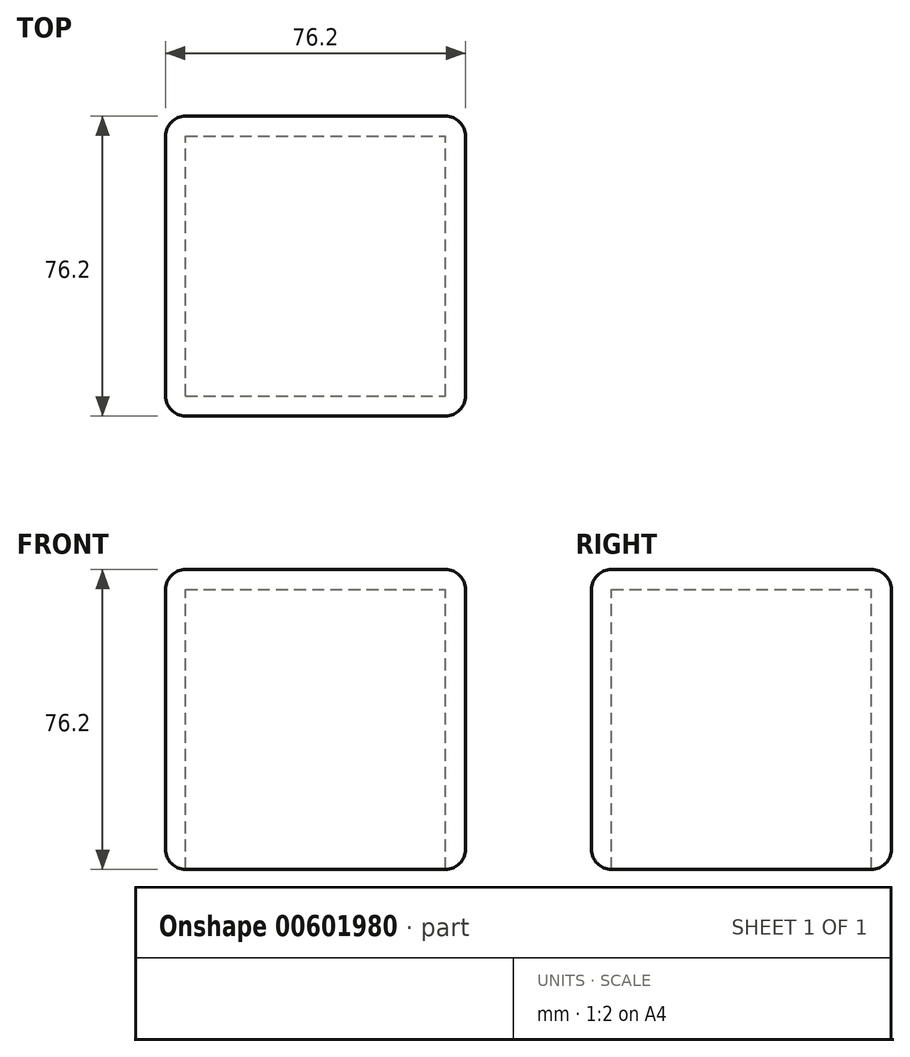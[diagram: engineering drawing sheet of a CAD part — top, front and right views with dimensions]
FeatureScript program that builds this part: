
annotation { "Feature Type Name" : "Feature", "Feature Type Description" : "" }
export const myFeature = defineFeature(function(context is Context, id is Id, definition is map)
    precondition{}
    {
        {
            var Q0;
            Q0=qCreatedBy(makeId("Front.planeOp"),FACE);
            var sketch = newSketch(context, id + "F0", { "sketchPlane" : qUnion([Q0])});
            skLineSegment(sketch, "E0.bottom", {"start": v(0, 0) * mm, "end": v(76.2, 0) * mm});
            skLineSegment(sketch, "E0.top", {"start": v(0, 76.2) * mm, "end": v(76.2, 76.2) * mm});
            skLineSegment(sketch, "E0.left", {"start": v(0, 0) * mm, "end": v(0, 76.2) * mm});
            skLineSegment(sketch, "E0.right", {"start": v(76.2, 0) * mm, "end": v(76.2, 76.2) * mm});
            skSolve(sketch);
        }
        {
            var Q0;
            Q0=makeQuery(id+"F0.imprint","IMPRINT",FACE,{"disambiguationData":[TD([[makeQuery(id+"F0.imprint","IMPRINT",EDGE,{"derivedFrom":sQuery(id+"F0.wireOp",EDGE,"E0.bottom")}),1.0]])]});
            extrude(context, id + "F1", {"entities" : qUnion([Q0]), "depth" : 76.2 * mm, "offsetDistance" : 25.4 * mm});
        }
        {
            var Q0;
            Q0=makeQuery(id+"F1.opExtrude","SWEPT_FACE",FACE,{"disambiguationData":[OSD([sQuery(id+"F0.wireOp",EDGE,"E0.bottom")])]});
            shell(context, id + "F2", {"entities" : qUnion([Q0]), "thickness" : 5.08 * mm});
        }
        {
            var Q0;
            Q0=makeQuery(id+"F1.opExtrude","SWEPT_FACE",FACE,{"disambiguationData":[OSD([sQuery(id+"F0.wireOp",EDGE,"E0.top")])]});
            var Q1;
            Q1=makeQuery(id+"F1.opExtrude","SWEPT_FACE",FACE,{"disambiguationData":[OSD([sQuery(id+"F0.wireOp",EDGE,"E0.right")])]});
            var Q2;
            Q2=makeQuery(id+"F1.opExtrude","CAP_EDGE",EDGE,{"disambiguationData":[OSD([sQuery(id+"F0.wireOp",EDGE,"E0.left")])],"isStart":true});
            var Q3;
            Q3=makeQuery(id+"F1.opExtrude","CAP_FACE",FACE,{"disambiguationData":[OSD([sQuery(id+"F0.wireOp",EDGE,"E0.bottom"),sQuery(id+"F0.wireOp",EDGE,"E0.top"),sQuery(id+"F0.wireOp",EDGE,"E0.left"),sQuery(id+"F0.wireOp",EDGE,"E0.right")])],"isStart":false});
            var Q4;
            Q4=makeQuery(id+"F1.opExtrude","SWEPT_EDGE",EDGE,{"disambiguationData":[OSD([sQuery(id+"F0.wireOp",EDGE,"E0.bottom"),sQuery(id+"F0.wireOp",EDGE,"E0.left")])]});
            var Q5;
            Q5=makeQuery(id+"F1.opExtrude","CAP_EDGE",EDGE,{"disambiguationData":[OSD([sQuery(id+"F0.wireOp",EDGE,"E0.bottom")])],"isStart":true});
            fillet(context, id + "F3", {"entities" : qUnion([Q0, Q1, Q2, Q3, Q4, Q5]), "radius" : 5.08 * mm, "tangentPropagation" : true, "allowEdgeOverflow" : false});
        }
    });
